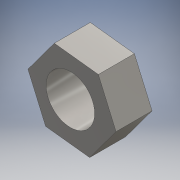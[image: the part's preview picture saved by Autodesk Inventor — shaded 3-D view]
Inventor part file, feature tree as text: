
AUTODESK INVENTOR PART (.ipt)
format: ipt  version: 2016 (Build 200138000, 138)  size: 114,688 bytes
history: native  units: mm
features: extrude x1, sketch x1
ambient origin geometry x8: Origin, YZ Plane, XZ Plane, XY Plane, X Axis, Y Axis, Z Axis, Center Point
bodies: Solid1 (feature_tree)
feature tree (2):
  extrude  "Extrusion1"  Depth=7.91mm
  sketch  "Sketch1"  dims[d0=5.0mm d1=7.91mm d2=3.71mm d3=0.0mm]
